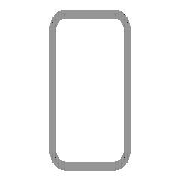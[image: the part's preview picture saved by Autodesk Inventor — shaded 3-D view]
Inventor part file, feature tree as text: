
AUTODESK INVENTOR PART (.ipt)
format: ipt  version: 2025.3 (Build 293356030, 356C)  size: 134,144 bytes
history: native  units: mm (DEFAULTED — no unit token found)
features: other x4, sketch x1, plane x1
ambient origin geometry x8: Origin, YZ Plane, XZ Plane, XY Plane, X Axis, Y Axis, Z Axis, Center Point
bodies: Solid1 (feature_tree), Body (feature_tree)
feature tree (6):
  parser-record x1  (decoder bookkeeping rows leaked as tree rows — omitted from the tree; the rows remain in map.json)
  other  "Driven Length"
  other  "Start Plane"
  other  "End Plane"
  sketch  "Sketch3"  dims[d3=1300.0mm d4=0.0mm d7=4.0mm d9=20.0mm d11=40.0mm d12=2.0mm d13=-0.0mm d14=1300.0mm d15=10.0mm d16=20.0mm d17=90.0deg d18=1300.0mm]
  plane  "Work Plane3"
